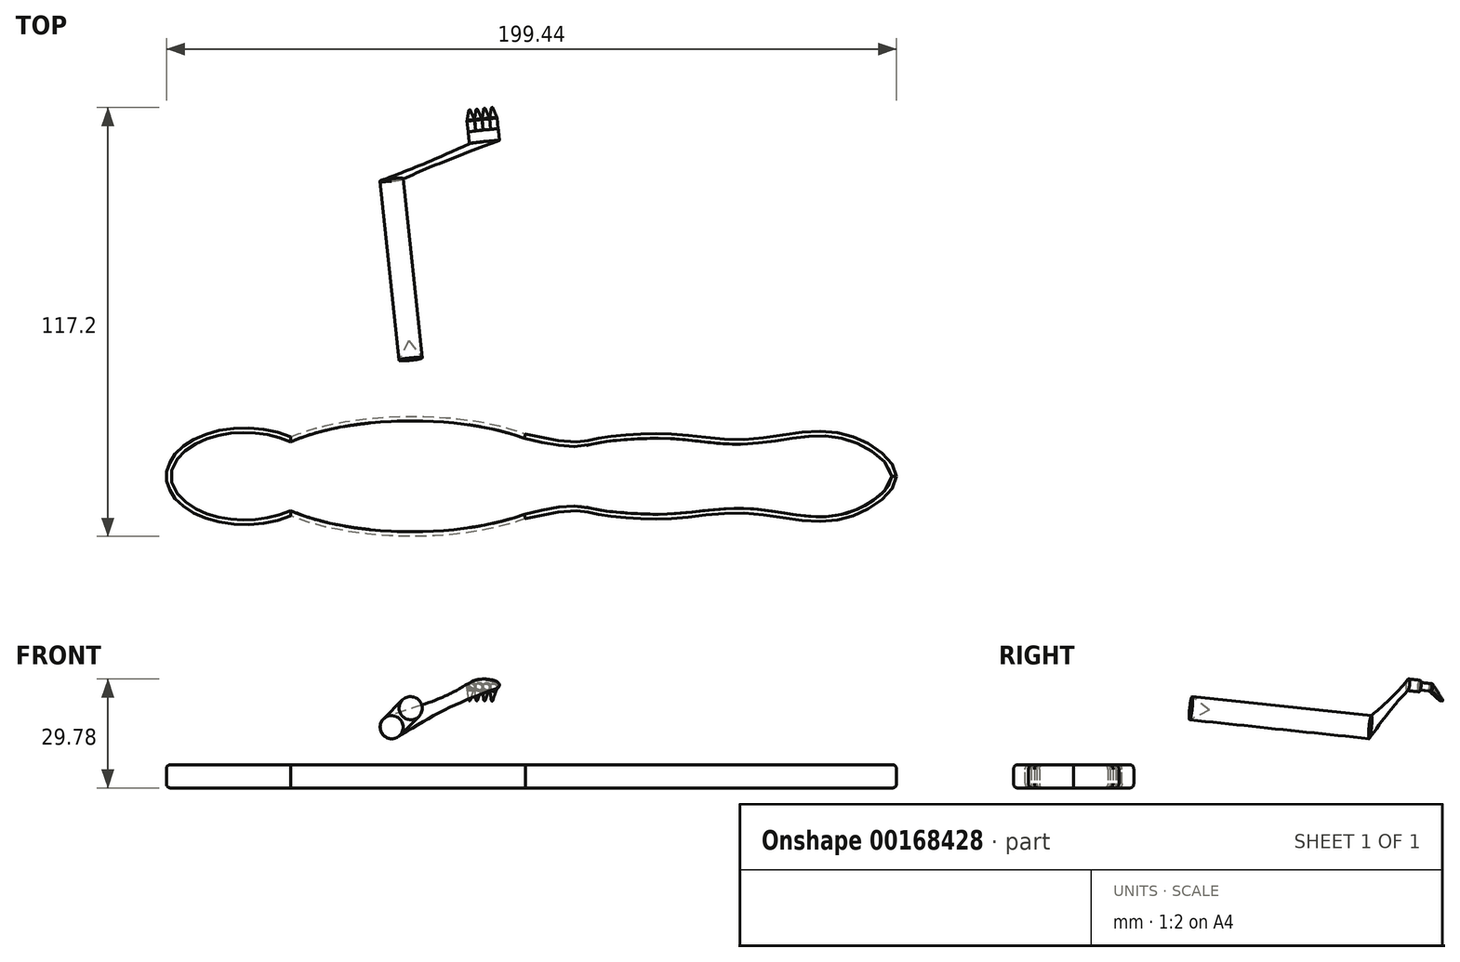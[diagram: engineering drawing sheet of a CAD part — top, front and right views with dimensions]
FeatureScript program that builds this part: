
annotation { "Feature Type Name" : "Feature", "Feature Type Description" : "" }
export const myFeature = defineFeature(function(context is Context, id is Id, definition is map)
    precondition{}
    {
        {
            var Q0;
            Q0=qCreatedBy(makeId("Top.planeOp"),FACE);
            var sketch = newSketch(context, id + "F0", { "sketchPlane" : qUnion([Q0])});
            skEllipse(sketch, "E0", {"center": v(-76.67, 0) * mm, "majorRadius": 21.44 * mm, "minorRadius": 13.23 * mm, "majorAxis": v(1, 0)});
            skSolve(sketch);
        }
        {
            var Q0;
            Q0=qCreatedBy(makeId("Top.planeOp"),FACE);
            var sketch = newSketch(context, id + "F1", { "sketchPlane" : qUnion([Q0])});
            skEllipse(sketch, "E1", {"center": v(-31.07, 0) * mm, "majorRadius": 43.84 * mm, "minorRadius": 16.42 * mm, "majorAxis": v(1, 0)});
            skSolve(sketch);
        }
        {
            var Q0;
            Q0=qCreatedBy(makeId("Top.planeOp"),FACE);
            var sketch = newSketch(context, id + "F2", { "sketchPlane" : qUnion([Q0])});
            skFitSpline(sketch, "E2", {"points": [v(0, 11.58) * mm, v(19, 10.26) * mm, v(29.1, 11.4) * mm, v(42.06, 11.4) * mm, v(60.16, 10.07) * mm, v(80.17, 12.36) * mm, v(94.27, 8.55) * mm, v(101.33, 0) * mm], "startDerivative": vector(258.74, -62.45) * mm, "endDerivative": vector(-0.5, -74.98) * mm});
            skFitSpline(sketch, "E3.MirrorCS", {"points": [v(0, -11.58) * mm, v(19, -10.26) * mm, v(29.1, -11.4) * mm, v(42.06, -11.4) * mm, v(60.16, -10.07) * mm, v(80.17, -12.36) * mm, v(94.27, -8.55) * mm, v(101.33, 0) * mm], "startDerivative": vector(258.74, 62.45) * mm, "endDerivative": vector(-0.5, 74.98) * mm});
            skLineSegment(sketch, "E4", {"start": v(0, -11.58) * mm, "end": v(0, 11.58) * mm});
            skSolve(sketch);
        }
        {
            var Q0;
            Q0=makeQuery(id+"F0.imprint","IMPRINT",FACE,{"disambiguationData":[TD([[makeQuery(id+"F0.imprint","IMPRINT",EDGE,{"derivedFrom":sQuery(id+"F0.wireOp",EDGE,"E0")}),1.0]])]});
            var Q1;
            Q1=makeQuery(id+"F1.imprint","IMPRINT",FACE,{"disambiguationData":[TD([[makeQuery(id+"F1.imprint","IMPRINT",EDGE,{"derivedFrom":sQuery(id+"F1.wireOp",EDGE,"E1")}),1.0]])]});
            var Q2;
            Q2=makeQuery(id+"F2.imprint","IMPRINT",FACE,{"disambiguationData":[TD([[makeQuery(id+"F2.imprint","IMPRINT",EDGE,{"derivedFrom":sQuery(id+"F2.wireOp",EDGE,"E2")}),-1.0]])]});
            extrude(context, id + "F3", {"entities" : qUnion([Q0, Q1, Q2]), "depth" : 6.35 * mm});
        }
        {
            var Q0;
            Q0=makeQuery(id+"F3.opExtrude","SWEPT_BODY",BODY,{"disambiguationData":[OSD([sQuery(id+"F0.wireOp",EDGE,"E0")])]});
            var Q1;
            Q1=makeQuery(id+"F3.opExtrude","SWEPT_BODY",BODY,{"disambiguationData":[OSD([sQuery(id+"F1.wireOp",EDGE,"E1")])]});
            var Q2;
            Q2=makeQuery(id+"F3.opExtrude","SWEPT_BODY",BODY,{"disambiguationData":[OSD([sQuery(id+"F2.wireOp",EDGE,"E2"),sQuery(id+"F2.wireOp",EDGE,"E3.MirrorCS"),sQuery(id+"F2.wireOp",EDGE,"E4")])]});
            booleanBodies(context, id + "F4", {"operationType" : BooleanOperationType.UNION, "tools" : qUnion([Q0, Q1, Q2])});
        }
        {
            var Q0;
            Q0=makeQuery(id+"F3.opExtrude","CAP_EDGE",EDGE,{"disambiguationData":[OSD([sQuery(id+"F2.wireOp",EDGE,"E2")])],"isStart":false});
            var Q1;
            {var subQ0=sQuery(id+"F1.wireOp",EDGE,"E1");var subQ2=sQuery(id+"F2.wireOp",EDGE,"E2");Q1=makeQuery(id+"F4.opBoolean","SPLIT",EDGE,{"disambiguationData":[TD([makeQuery(id+"F3.opExtrude","SWEPT_FACE",FACE,{"disambiguationData":[OSD([subQ2])]})])],"derivedFrom":makeQuery(id+"F3.opExtrude","CAP_EDGE",EDGE,{"disambiguationData":[OSD([subQ0])],"isStart":false})});}
            var Q2;
            {var subQ0=sQuery(id+"F1.wireOp",EDGE,"E1");var subQ2=sQuery(id+"F2.wireOp",EDGE,"E2");Q2=makeQuery(id+"F4.opBoolean","SPLIT",EDGE,{"disambiguationData":[TD([makeQuery(id+"F3.opExtrude","SWEPT_FACE",FACE,{"disambiguationData":[OSD([subQ2])]})])],"derivedFrom":makeQuery(id+"F3.opExtrude","CAP_EDGE",EDGE,{"disambiguationData":[OSD([subQ0])],"isStart":true})});}
            var Q3;
            Q3=makeQuery(id+"F3.opExtrude","CAP_EDGE",EDGE,{"disambiguationData":[OSD([sQuery(id+"F2.wireOp",EDGE,"E2")])],"isStart":true});
            var Q4;
            {var subQ0=sQuery(id+"F1.wireOp",EDGE,"E1");var subQ2=sQuery(id+"F2.wireOp",EDGE,"E3.MirrorCS");Q4=makeQuery(id+"F4.opBoolean","SPLIT",EDGE,{"disambiguationData":[TD([makeQuery(id+"F3.opExtrude","SWEPT_FACE",FACE,{"disambiguationData":[OSD([subQ2])]})])],"derivedFrom":makeQuery(id+"F3.opExtrude","CAP_EDGE",EDGE,{"disambiguationData":[OSD([subQ0])],"isStart":false})});}
            var Q5;
            {var subQ0=sQuery(id+"F1.wireOp",EDGE,"E1");var subQ2=sQuery(id+"F2.wireOp",EDGE,"E3.MirrorCS");Q5=makeQuery(id+"F4.opBoolean","SPLIT",EDGE,{"disambiguationData":[TD([makeQuery(id+"F3.opExtrude","SWEPT_FACE",FACE,{"disambiguationData":[OSD([subQ2])]})])],"derivedFrom":makeQuery(id+"F3.opExtrude","CAP_EDGE",EDGE,{"disambiguationData":[OSD([subQ0])],"isStart":true})});}
            var Q6;
            Q6=makeQuery(id+"F3.opExtrude","CAP_EDGE",EDGE,{"disambiguationData":[OSD([sQuery(id+"F0.wireOp",EDGE,"E0")])],"isStart":true});
            var Q7;
            Q7=makeQuery(id+"F3.opExtrude","CAP_EDGE",EDGE,{"disambiguationData":[OSD([sQuery(id+"F0.wireOp",EDGE,"E0")])],"isStart":false});
            fillet(context, id + "F5", {"entities" : qUnion([Q0, Q1, Q2, Q3, Q4, Q5, Q6, Q7]), "radius" : 1.27 * mm, "tangentPropagation" : true, "rho" : 0.5, "crossSection" : FilletCrossSection.CONIC, "allowEdgeOverflow" : false});
        }
        {
            var Q0;
            Q0=qCreatedBy(makeId("Top.planeOp"),FACE);
            var sketch = newSketch(context, id + "F6", { "sketchPlane" : qUnion([Q0])});
            skLineSegment(sketch, "E5", {"start": v(-53.17, 0) * mm, "end": v(-53.17, -7.62) * mm, "construction": true});
            skSolve(sketch);
        }
        {
            var Q0;
            Q0=makeQuery(id+"F4.opBoolean","MERGE",FACE,{"derivedFrom":[makeQuery(id+"F3.opExtrude","CAP_FACE",FACE,{"disambiguationData":[OSD([sQuery(id+"F0.wireOp",EDGE,"E0")])],"isStart":true}),makeQuery(id+"F3.opExtrude","CAP_FACE",FACE,{"disambiguationData":[OSD([sQuery(id+"F1.wireOp",EDGE,"E1")])],"isStart":true}),makeQuery(id+"F3.opExtrude","CAP_FACE",FACE,{"disambiguationData":[OSD([sQuery(id+"F2.wireOp",EDGE,"E2"),sQuery(id+"F2.wireOp",EDGE,"E3.MirrorCS"),sQuery(id+"F2.wireOp",EDGE,"E4")])],"isStart":true})]});
            var Q1;
            Q1=sQuery(id+"F6.wireOp",EDGE,"E5");
            cPlane(context, id + "F7", {"entities" : qUnion([Q0, Q1]), "cplaneType" : CPlaneType.LINE_ANGLE, "offset" : 25.4 * mm, "angle" : 45 * degree, "width" : 152.4 * mm, "height" : 152.4 * mm});
        }
        {
            var Q0;
            Q0=qCreatedBy(id+"F7.planeOp",FACE);
            var sketch = newSketch(context, id + "F8", { "sketchPlane" : qUnion([Q0])});
            skLineSegment(sketch, "E6", {"start": v(-37.06, -7.53) * mm, "end": v(-81.02, -14.1) * mm});
            skLineSegment(sketch, "E7", {"start": v(-81.02, -14.1) * mm, "end": v(-81.49, -10.96) * mm});
            skLineSegment(sketch, "E8", {"start": v(-81.49, -10.96) * mm, "end": v(-32.5, -3.64) * mm});
            skLineSegment(sketch, "E9", {"start": v(-32.5, -3.64) * mm, "end": v(-37.06, -7.53) * mm});
            skLineSegment(sketch, "E10", {"start": v(-81.49, -10.96) * mm, "end": v(-84.63, -11.43) * mm, "construction": true});
            skLineSegment(sketch, "E11", {"start": v(-84.63, -11.43) * mm, "end": v(-84.4, -13) * mm, "construction": true});
            skSolve(sketch);
        }
        {
            var Q0;
            Q0=makeQuery(id+"F8.imprint","IMPRINT",FACE,{"disambiguationData":[TD([[makeQuery(id+"F8.imprint","IMPRINT",EDGE,{"derivedFrom":sQuery(id+"F8.wireOp",EDGE,"E6")}),-1.0]])]});
            var Q1;
            Q1=sQuery(id+"F8.wireOp",EDGE,"E6");
            revolve(context, id + "F9", {"operationType" : NewBodyOperationType.ADD, "entities" : qUnion([Q0]), "axis" : qUnion([Q1]), "revolveType" : RevolveType.FULL});
        }
        {
            var Q0;
            Q0=makeQuery(id+"F9.opRevolve","SWEPT_FACE",FACE,{"disambiguationData":[OSD([sQuery(id+"F8.wireOp",EDGE,"E7")])]});
            cPlane(context, id + "F10", {"entities" : qUnion([Q0]), "cplaneType" : CPlaneType.OFFSET, "offset" : 6.35 * mm, "width" : 152.4 * mm, "height" : 152.4 * mm});
        }
        {
            var Q0;
            Q0=qCreatedBy(id+"F10.planeOp",FACE);
            var sketch = newSketch(context, id + "F11", { "sketchPlane" : qUnion([Q0])});
            skEllipse(sketch, "E12", {"center": v(1.97, 37.65) * mm, "majorRadius": 4.13 * mm, "minorRadius": 1.6 * mm, "majorAxis": v(-1, 0)});
            skSolve(sketch);
        }
        {
            var Q0;
            Q0=makeQuery(id+"F11.imprint","IMPRINT",FACE,{"disambiguationData":[TD([[makeQuery(id+"F11.imprint","IMPRINT",EDGE,{"derivedFrom":sQuery(id+"F11.wireOp",EDGE,"E12")}),1.0]])]});
            extrude(context, id + "F12", {"entities" : qUnion([Q0]), "depth" : 3.17 * mm});
        }
        {
            var Q0;
            Q0=makeQuery(id+"F9.opRevolve","SWEPT_FACE",FACE,{"disambiguationData":[OSD([sQuery(id+"F8.wireOp",EDGE,"E7")])]});
            var Q1;
            Q1=makeQuery(id+"F12.opExtrude","CAP_FACE",FACE,{"disambiguationData":[OSD([sQuery(id+"F11.wireOp",EDGE,"E12")])],"isStart":true});
            loft(context, id + "F13", {"sheetProfilesArray" : [{ "sheetProfileEntities" : qUnion([Q0]) }, { "sheetProfileEntities" : qUnion([Q1]) }]});
        }
        {
            var Q0;
            Q0=qCreatedBy(id+"F10.planeOp",FACE);
            cPlane(context, id + "F14", {"entities" : qUnion([Q0]), "cplaneType" : CPlaneType.OFFSET, "offset" : 3.17 * mm, "width" : 152.4 * mm, "height" : 152.4 * mm});
        }
        {
            var Q0;
            Q0=qCreatedBy(id+"F14.planeOp",FACE);
            var sketch = newSketch(context, id + "F15", { "sketchPlane" : qUnion([Q0])});
            skLineSegment(sketch, "E13", {"start": v(1.98, 37.6) * mm, "end": v(0.94, 37.6) * mm, "construction": true});
            skLineSegment(sketch, "E14", {"start": v(0.94, 37.6) * mm, "end": v(-1.12, 37.6) * mm, "construction": true});
            skLineSegment(sketch, "E15", {"start": v(1.98, 37.6) * mm, "end": v(3, 37.6) * mm, "construction": true});
            skLineSegment(sketch, "E16", {"start": v(3, 37.6) * mm, "end": v(5.07, 37.6) * mm, "construction": true});
            skCircle(sketch, "E17", {"center": v(-1.12, 37.6) * mm, "radius": 1.03 * mm});
            skCircle(sketch, "E18", {"center": v(0.94, 37.6) * mm, "radius": 1.02 * mm});
            skCircle(sketch, "E19", {"center": v(3, 37.6) * mm, "radius": 1.02 * mm});
            skCircle(sketch, "E20", {"center": v(5.07, 37.6) * mm, "radius": 1.03 * mm});
            skSolve(sketch);
        }
        {
            var Q0;
            Q0=makeQuery(id+"F15.imprint","IMPRINT",FACE,{"disambiguationData":[TD([[makeQuery(id+"F15.imprint","IMPRINT",EDGE,{"derivedFrom":sQuery(id+"F15.wireOp",EDGE,"E17")}),1.0]])]});
            var Q1;
            {var subQ0=sQuery(id+"F15.wireOp",EDGE,"E18");var subQ1=makeQuery(id+"F15.imprint","INTERSECT",VERTEX,{"derivedFrom":[sQuery(id+"F15.wireOp",EDGE,"E17"),subQ0]});Q1=makeQuery(id+"F15.imprint","IMPRINT",FACE,{"disambiguationData":[TD([[makeQuery(id+"F15.imprint","IMPRINT",EDGE,{"disambiguationData":[TD([[subQ1,1.0]])],"derivedFrom":subQ0}),1.0]])]});}
            var Q2;
            {var subQ0=sQuery(id+"F15.wireOp",EDGE,"E19");var subQ1=makeQuery(id+"F15.imprint","INTERSECT",VERTEX,{"derivedFrom":[sQuery(id+"F15.wireOp",EDGE,"E18"),subQ0]});Q2=makeQuery(id+"F15.imprint","IMPRINT",FACE,{"disambiguationData":[TD([[makeQuery(id+"F15.imprint","IMPRINT",EDGE,{"disambiguationData":[TD([[subQ1,1.0]])],"derivedFrom":subQ0}),1.0]])]});}
            var Q3;
            Q3=makeQuery(id+"F15.imprint","IMPRINT",FACE,{"disambiguationData":[TD([[makeQuery(id+"F15.imprint","IMPRINT",EDGE,{"derivedFrom":sQuery(id+"F15.wireOp",EDGE,"E20")}),1.0]])]});
            var Q4;
            Q4=makeQuery(id+"F15.imprint","IMPRINT",FACE,{"disambiguationData":[TD([[makeQuery(id+"F15.imprint","IMPRINT",EDGE,{"derivedFrom":sQuery(id+"F15.wireOp",EDGE,"E18")}),1.0]])]});
            var Q5;
            Q5=makeQuery(id+"F15.imprint","IMPRINT",FACE,{"disambiguationData":[TD([[makeQuery(id+"F15.imprint","IMPRINT",EDGE,{"derivedFrom":sQuery(id+"F15.wireOp",EDGE,"E19")}),1.0]])]});
            extrude(context, id + "F16", {"entities" : qUnion([Q0, Q1, Q2, Q3, Q4, Q5]), "depth" : 3.17 * mm});
        }
        {
            var Q0;
            Q0=qCreatedBy(id+"F14.planeOp",FACE);
            cPlane(context, id + "F17", {"entities" : qUnion([Q0]), "cplaneType" : CPlaneType.OFFSET, "offset" : 3.17 * mm, "width" : 152.4 * mm, "height" : 152.4 * mm});
        }
        {
            var Q0;
            Q0=qCreatedBy(id+"F17.planeOp",FACE);
            cPlane(context, id + "F18", {"entities" : qUnion([Q0]), "cplaneType" : CPlaneType.OFFSET, "offset" : 3.17 * mm, "width" : 152.4 * mm, "height" : 152.4 * mm});
        }
        {
            var Q0;
            Q0=qCreatedBy(id+"F18.planeOp",FACE);
            var sketch = newSketch(context, id + "F19", { "sketchPlane" : qUnion([Q0])});
            skLineSegment(sketch, "E21", {"start": v(0.94, 37.6) * mm, "end": v(0.94, 34.42) * mm, "construction": true});
            skLineSegment(sketch, "E22", {"start": v(-1.12, 37.6) * mm, "end": v(-1.12, 34.42) * mm, "construction": true});
            skLineSegment(sketch, "E23", {"start": v(3, 37.6) * mm, "end": v(3.08, 34.42) * mm, "construction": true});
            skLineSegment(sketch, "E24", {"start": v(5.07, 37.6) * mm, "end": v(5.07, 34.42) * mm});
            skCircle(sketch, "E25", {"center": v(-1.12, 34.42) * mm, "radius": 0.2 * mm});
            skCircle(sketch, "E26", {"center": v(0.94, 34.42) * mm, "radius": 0.2 * mm});
            skCircle(sketch, "E27", {"center": v(3.08, 34.42) * mm, "radius": 0.2 * mm});
            skCircle(sketch, "E28", {"center": v(5.07, 34.42) * mm, "radius": 0.2 * mm});
            skSolve(sketch);
        }
        {
            var Q0;
            Q0=makeQuery(id+"F16.opExtrude","CAP_FACE",FACE,{"disambiguationData":[OSD([sQuery(id+"F15.wireOp",EDGE,"E17")])],"isStart":false});
            var Q1;
            Q1=makeQuery(id+"F19.imprint","IMPRINT",FACE,{"disambiguationData":[TD([[makeQuery(id+"F19.imprint","IMPRINT",EDGE,{"derivedFrom":sQuery(id+"F19.wireOp",EDGE,"E25")}),1.0]])]});
            loft(context, id + "F20", {"sheetProfilesArray" : [{ "sheetProfileEntities" : qUnion([Q0]) }, { "sheetProfileEntities" : qUnion([Q1]) }]});
        }
        {
            var Q0;
            Q0=makeQuery(id+"F16.opExtrude","CAP_FACE",FACE,{"disambiguationData":[OSD([sQuery(id+"F15.wireOp",EDGE,"E18")])],"isStart":false});
            var Q1;
            Q1=makeQuery(id+"F19.imprint","IMPRINT",FACE,{"disambiguationData":[TD([[makeQuery(id+"F19.imprint","IMPRINT",EDGE,{"derivedFrom":sQuery(id+"F19.wireOp",EDGE,"E26")}),1.0]])]});
            loft(context, id + "F21", {"sheetProfilesArray" : [{ "sheetProfileEntities" : qUnion([Q0]) }, { "sheetProfileEntities" : qUnion([Q1]) }]});
        }
        {
            var Q0;
            Q0=makeQuery(id+"F16.opExtrude","CAP_FACE",FACE,{"disambiguationData":[OSD([sQuery(id+"F15.wireOp",EDGE,"E19")])],"isStart":false});
            var Q1;
            Q1=makeQuery(id+"F19.imprint","IMPRINT",FACE,{"disambiguationData":[TD([[makeQuery(id+"F19.imprint","IMPRINT",EDGE,{"derivedFrom":sQuery(id+"F19.wireOp",EDGE,"E27")}),1.0]])]});
            loft(context, id + "F22", {"sheetProfilesArray" : [{ "sheetProfileEntities" : qUnion([Q0]) }, { "sheetProfileEntities" : qUnion([Q1]) }]});
        }
        {
            var Q0;
            Q0=makeQuery(id+"F16.opExtrude","CAP_FACE",FACE,{"disambiguationData":[OSD([sQuery(id+"F15.wireOp",EDGE,"E20")])],"isStart":false});
            var Q1;
            Q1=makeQuery(id+"F19.imprint","IMPRINT",FACE,{"disambiguationData":[TD([[makeQuery(id+"F19.imprint","IMPRINT",EDGE,{"derivedFrom":sQuery(id+"F19.wireOp",EDGE,"E28")}),1.0]])]});
            loft(context, id + "F23", {"sheetProfilesArray" : [{ "sheetProfileEntities" : qUnion([Q0]) }, { "sheetProfileEntities" : qUnion([Q1]) }]});
        }
        {
            var Q0;
            Q0=makeQuery(id+"F3.opExtrude","SWEPT_BODY",BODY,{"disambiguationData":[OSD([sQuery(id+"F0.wireOp",EDGE,"E0")])]});
            var Q1;
            Q1=qCreatedBy(makeId("Front.planeOp"),FACE);
            mirror(context, id + "F24", {"operationType" : NewBodyOperationType.ADD, "entities" : qUnion([Q0]), "mirrorPlane" : qUnion([Q1])});
        }
    });
